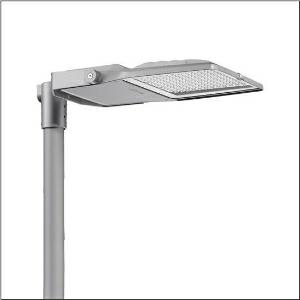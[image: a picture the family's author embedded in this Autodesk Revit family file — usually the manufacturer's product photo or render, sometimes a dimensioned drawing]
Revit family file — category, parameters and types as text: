
# Revit family: floodlight_fl_21_iq_midi___pl52_5xa7781e4d3a_f0c1
name_source: partatom
category: Lighting Fixtures
units: mm (PartAtom-declared; Revit-internal decimal feet)

## family parameters
Cut with Voids When Loaded = No
Host = Face
Light Source = No
Part Type = Normal
Room Calculation Point = No
Round Connector Dimension = Use Diameter
Shared = No

## types (1)
- --- (1 x LED, 28010 lm, 208.1 W, 4000K)
    Apparent Load = 208 VA
    CIE Flux Codes = 26 60 98 100 100
    Color Rendering = 70
    Color Temperature = 4000K
    Default Elevation = 1800 mm
    Description = Floodlight FL 21 iQ midi, floodlight, primary light control with lens, of PMMA, primary optical cover: protective disc, of toughened safety glass, transparent, light distribution: PL52, light emission: direct distribution, installation type: surface-mounted, lamps: LED, High Power LED, rated values: 28.010lm | 208,1W | 134,6lm/W (begin service life); end service life: 28.010lm | 227,1W; at 50% lumin. flux: 14.005lm | 90,3W | 155,1lm/W, colour temperature: 4000K, colour rendering: CRI > 70, light colour: 740, light setting 1 begin service life: 100% | 28.010lm | 208,1W | 134,6lm/W | 4.000K, light setting 1 end service life: 227,1W, further light settings possible, control: optimised constant luminous flux control (CLO 2.0), Desk-Remote (wireless, voltage-free reading and setting of iQ features in the workshop via application-optimized NFC function/RFID function), Light-Fading, Smart-Wire, Night-Set, Lumen-Switch, Temp-Guard, Auto-Match, pre-setting: linear dimming characteristic, with terminal, 6-pole, mains connection: 220..240V, AC, 50/60Hz, luminaire housing, of diecast aluminium, powder-coated, SITECO metallic grey (DB 702S), corrosivity category C5 mid according to DIN EN ISO 12944suitable for swimming poolschlorine-resistant, sealing non-destructively replaceable, please order mast flange separately, mast bracket, of steel, galvanised, powder-coated, SITECO metallic grey (DB 702S), protection rating (complete): IP66, insulation class (complete): insulation class II (safety insulation), certification: CE, ENEC, VDE, protection symbol: D, impact resistance: IK08, permissible operating ambient temperature: -40..+40°C, permissible operating ambient temperature for outdoor applications: -40..+50°C, standard: DIN EN 12944, LABS conformity tested according to VDMA 24364:2018-05, packaging unit: 1 piece

Light Distribution: PL52
    Height = 76 mm
    Lamp = 1 x LED
    Lamp Light Flux = 28010 lm
    Lamp Power = 208.1 W
    Lamp count = 1
    Length = 657 mm
    Luminous efficacy = 135 lm/W
    Manufacturer = Siteco
    ModVariant = No
    Model = 5XA7781E4D3A
    Number of Poles = 1
    OnlyDefault = Yes
    Power Factor = 1
    Product Name = Floodlight FL 21 iQ midi | PL52
    Product group = floodlight | pylon annexe
    ProductGroupID = 6201
    Protection Class = Protection class II
    Protection Degree = IP 66
    RLX_Detail_Level = 1
    RLX_Emergency_Light_Flux = 0 lm
    RLX_Emergency_Type = 0
    RLX_Emergency_Type_DB = No
    RlxData = <blob elided: 154113 chars, md5=facbcd6a>
    Socket = socket
    Standby Power = 0 W
    System Light Flux = 28010 lm
    System Power = 208 W
    Type Comments = factory setting: luminous flux: 100 % | dim-lin: 254 | 710 mA
    Type Image = l_1007123.jpg
    URL = http://relux.com
    VarID = @adj_106145
    Voltage = 0 V
    Weight = 0.00 kg
    Width = 442 mm

## geometry (parser evidence)
native form markers: Blend x4, Sweep x15
no freeform markers — native parametric forms only
